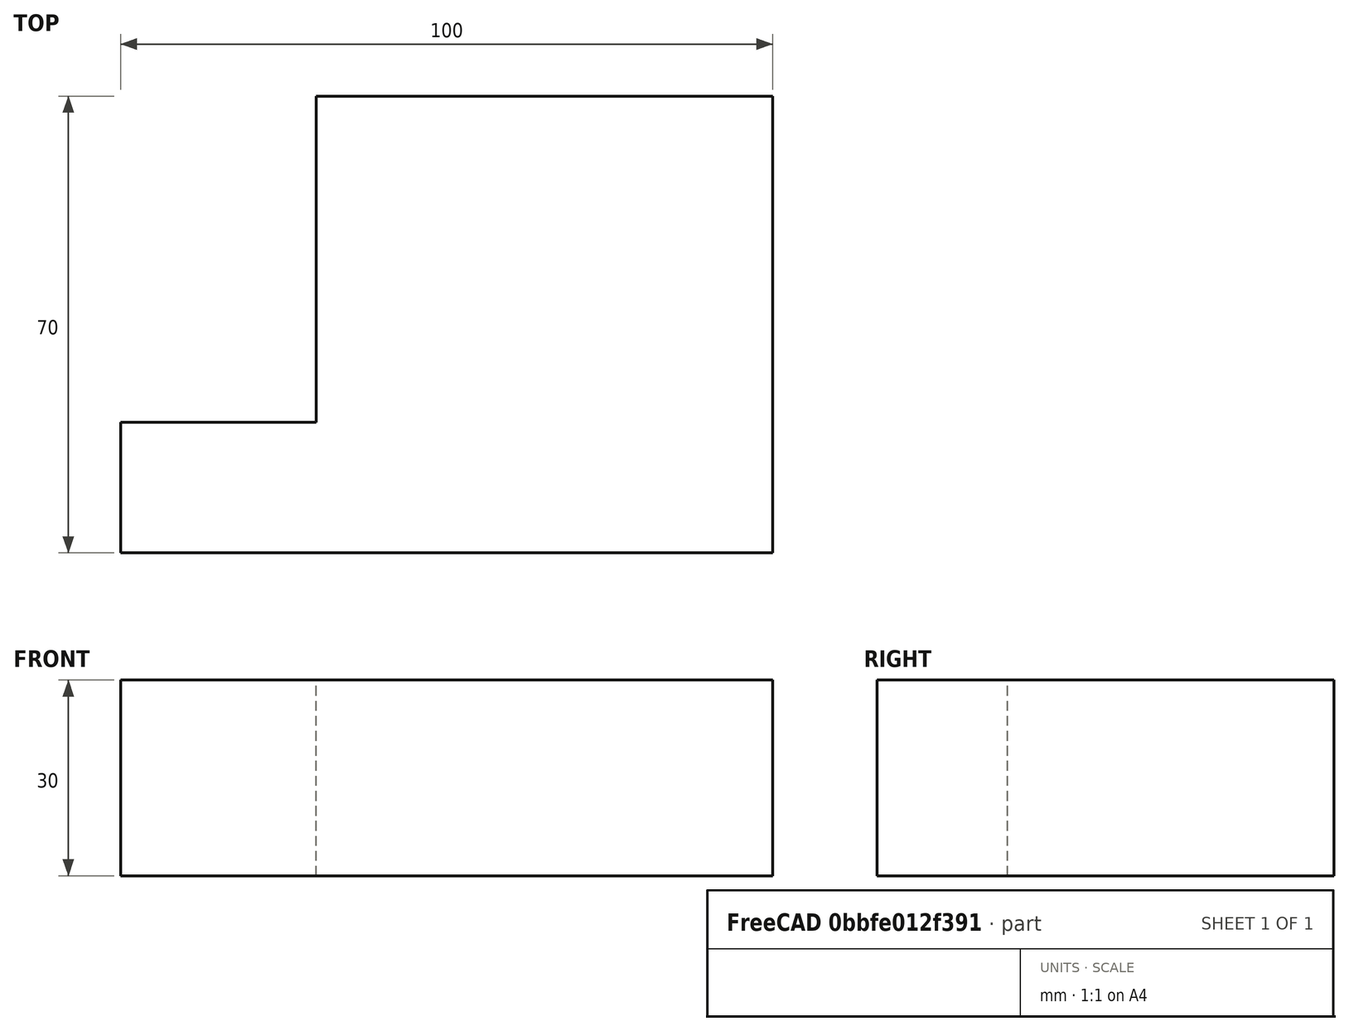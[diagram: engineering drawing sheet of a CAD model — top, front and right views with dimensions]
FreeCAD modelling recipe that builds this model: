
FCSTD DOCUMENT  (FreeCAD 0.19R24276 (Git))
Label: Opora_100x30_v1
License: All rights reserved
LicenseURL: http://en.wikipedia.org/wiki/All_rights_reserved
objects: Sketcher::SketchObject×1, PartDesign::Pad×1, PartDesign::Body×1
note: 4 computed .brp shape members not serialized (recipe doc carries the construction recipe); baked Part::Feature solids carry a one-line shape summary decoded from their .brp

FEATURE [Sketcher::SketchObject] Sketch
  FullyConstrained = false
  MapMode = 5
  Support = -> [XY_Plane]
  sketch-geometry (6):
    g0: LineSegment StartX=0 StartY=0 StartZ=0 EndX=100 EndY=0 EndZ=0
    g1: LineSegment StartX=100 StartY=0 StartZ=0 EndX=100 EndY=70 EndZ=0
    g2: LineSegment StartX=100 StartY=70 StartZ=0 EndX=30 EndY=70 EndZ=0
    g3: LineSegment StartX=0 StartY=20 StartZ=0 EndX=0 EndY=0 EndZ=0
    g4: LineSegment StartX=30 StartY=70 StartZ=0 EndX=30 EndY=20 EndZ=0
    g5: LineSegment StartX=30 StartY=20 StartZ=0 EndX=0 EndY=20 EndZ=0
  constraints (16):
    c: Coincident(g0,g1)
    c: Coincident(g1,g2)
    c: Coincident(g3,g0)
    c: Horizontal(g0)
    c: Horizontal(g2)
    c: Vertical(g1)
    c: Vertical(g3)
    c: Coincident(g0,g-1)
    c: DistanceY(g1,g1) = 70
    c: DistanceX(g0,g0) = 100
    c: Coincident(g4,g5)
    c: Horizontal(g5)
    c: Vertical(g4)
    c: DistanceY(g4,g4) = 50
    c: DistanceX(g5,g5) = 30
    c: PointOnObject(g3,g5)
FEATURE [PartDesign::Pad] Pad
  Direction = (1,1,1)
  Length = 30
  Length2 = 100
  Profile = -> Sketch
  Type = 0
FEATURE [PartDesign::Body] Body
  Group = -> [Sketch,Pad]
  Origin = -> Origin
  Tip = -> Pad
